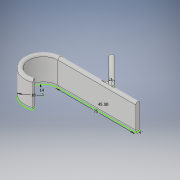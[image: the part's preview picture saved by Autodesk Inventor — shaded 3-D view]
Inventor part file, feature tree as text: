
AUTODESK INVENTOR PART (.ipt)
format: ipt  version: 2019 (Build 230136000, 136)  size: 402,432 bytes
history: native  units: mm
features: sketch x4, extrude x2, fillet x2
ambient origin geometry x8: Origin, YZ Plane, XZ Plane, XY Plane, X Axis, Y Axis, Z Axis, Center Point
bodies: Solid1 (feature_tree)
feature tree (8):
  extrude  "Extrusion1"  Depth=18.0mm
  fillet  "Fillet1"  Radius=18.0mm
  fillet  "Fillet2"  [1 undecoded]
  sketch  "Sketch2"  dims[d7=4.0mm d8=4.0mm]
  sketch  "Sketch3"  dims[d9=25.0mm d10=0.0mm]
  extrude  "Extrusion2"  Depth=4.0mm
  sketch  "Sketch1"  dims[d3=75.0mm d4=14.0mm d5=18.0mm d6=45.0deg]
  sketch  "Sketch4"  dims[d11=2.0mm d12=2.0mm d13=1.0mm d14=5.0mm d15=0.0mm d16=0.0mm]
note: 1 required parameter value undecoded (feature->parameter linkage not recoverable at this tier; creation-order binding heuristic only, values carry confidence <= 0.55)
